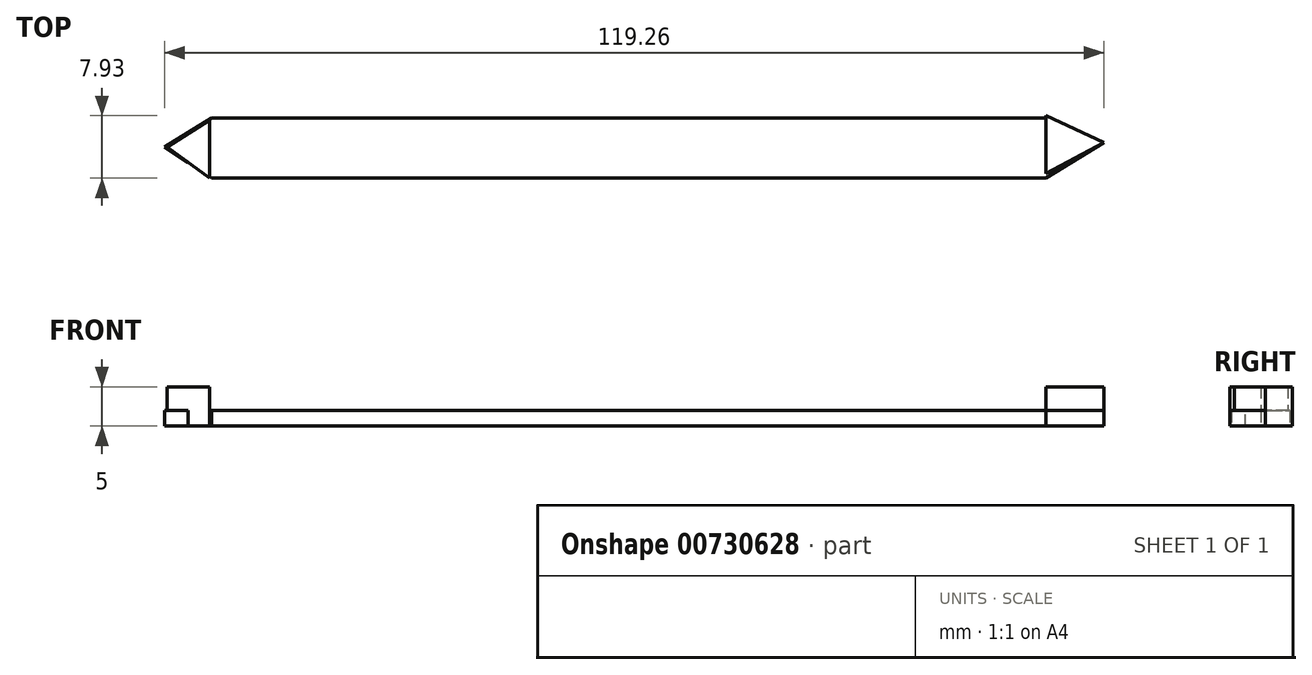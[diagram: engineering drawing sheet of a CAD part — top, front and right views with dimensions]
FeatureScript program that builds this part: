
annotation { "Feature Type Name" : "Feature", "Feature Type Description" : "" }
export const myFeature = defineFeature(function(context is Context, id is Id, definition is map)
    precondition{}
    {
        {
            var Q0;
            Q0=qCreatedBy(makeId("Top.planeOp"),FACE);
            var sketch = newSketch(context, id + "F0", { "sketchPlane" : qUnion([Q0])});
            skLineSegment(sketch, "E0.bottom", {"start": v(-58.21, 14.59) * mm, "end": v(47.73, 14.59) * mm});
            skLineSegment(sketch, "E0.top", {"start": v(-58.21, 6.94) * mm, "end": v(47.73, 6.94) * mm});
            skLineSegment(sketch, "E1", {"start": v(-58.21, 14.59) * mm, "end": v(-64.16, 10.9) * mm});
            skLineSegment(sketch, "E2", {"start": v(-64.16, 10.9) * mm, "end": v(-58.21, 6.94) * mm});
            skLineSegment(sketch, "E3", {"start": v(47.73, 14.59) * mm, "end": v(55.1, 11.47) * mm});
            skLineSegment(sketch, "E4", {"start": v(55.1, 11.47) * mm, "end": v(47.73, 6.94) * mm});
            skSolve(sketch);
        }
        {
            var Q0;
            Q0=makeQuery(id+"F0.imprint","IMPRINT",FACE,{"disambiguationData":[TD([[makeQuery(id+"F0.imprint","IMPRINT",EDGE,{"derivedFrom":sQuery(id+"F0.wireOp",EDGE,"E0.bottom")}),-1.0]])]});
            extrude(context, id + "F1", {"entities" : qUnion([Q0]), "depth" : 2 * mm, "offsetDistance" : 25 * mm});
        }
        {
            var Q0;
            Q0=qCreatedBy(makeId("Top.planeOp"),FACE);
            var sketch = newSketch(context, id + "F2", { "sketchPlane" : qUnion([Q0])});
            skLineSegment(sketch, "E5", {"start": v(-63.88, 10.9) * mm, "end": v(-58.5, 14.3) * mm});
            skLineSegment(sketch, "E6", {"start": v(-58.5, 14.3) * mm, "end": v(-58.5, 6.94) * mm});
            skLineSegment(sketch, "E7", {"start": v(-58.5, 6.94) * mm, "end": v(-63.88, 10.9) * mm});
            skSolve(sketch);
        }
        {
            var Q0;
            Q0 = qSketchRegion(id + "F2", true);
            extrude(context, id + "F3", {"entities" : qUnion([Q0]), "operationType" : NewBodyOperationType.ADD, "depth" : 5 * mm, "offsetDistance" : 25 * mm});
        }
        {
            var Q0;
            Q0=qCreatedBy(makeId("Top.planeOp"),FACE);
            var sketch = newSketch(context, id + "F4", { "sketchPlane" : qUnion([Q0])});
            skLineSegment(sketch, "E8", {"start": v(47.73, 14.87) * mm, "end": v(47.73, 7.5) * mm});
            skLineSegment(sketch, "E9", {"start": v(47.73, 7.5) * mm, "end": v(55.1, 11.47) * mm});
            skLineSegment(sketch, "E10", {"start": v(55.1, 11.47) * mm, "end": v(47.73, 14.87) * mm});
            skSolve(sketch);
        }
        {
            var Q0;
            Q0 = qSketchRegion(id + "F4", true);
            extrude(context, id + "F5", {"entities" : qUnion([Q0]), "operationType" : NewBodyOperationType.ADD, "depth" : 5 * mm, "offsetDistance" : 25 * mm});
        }
    });
